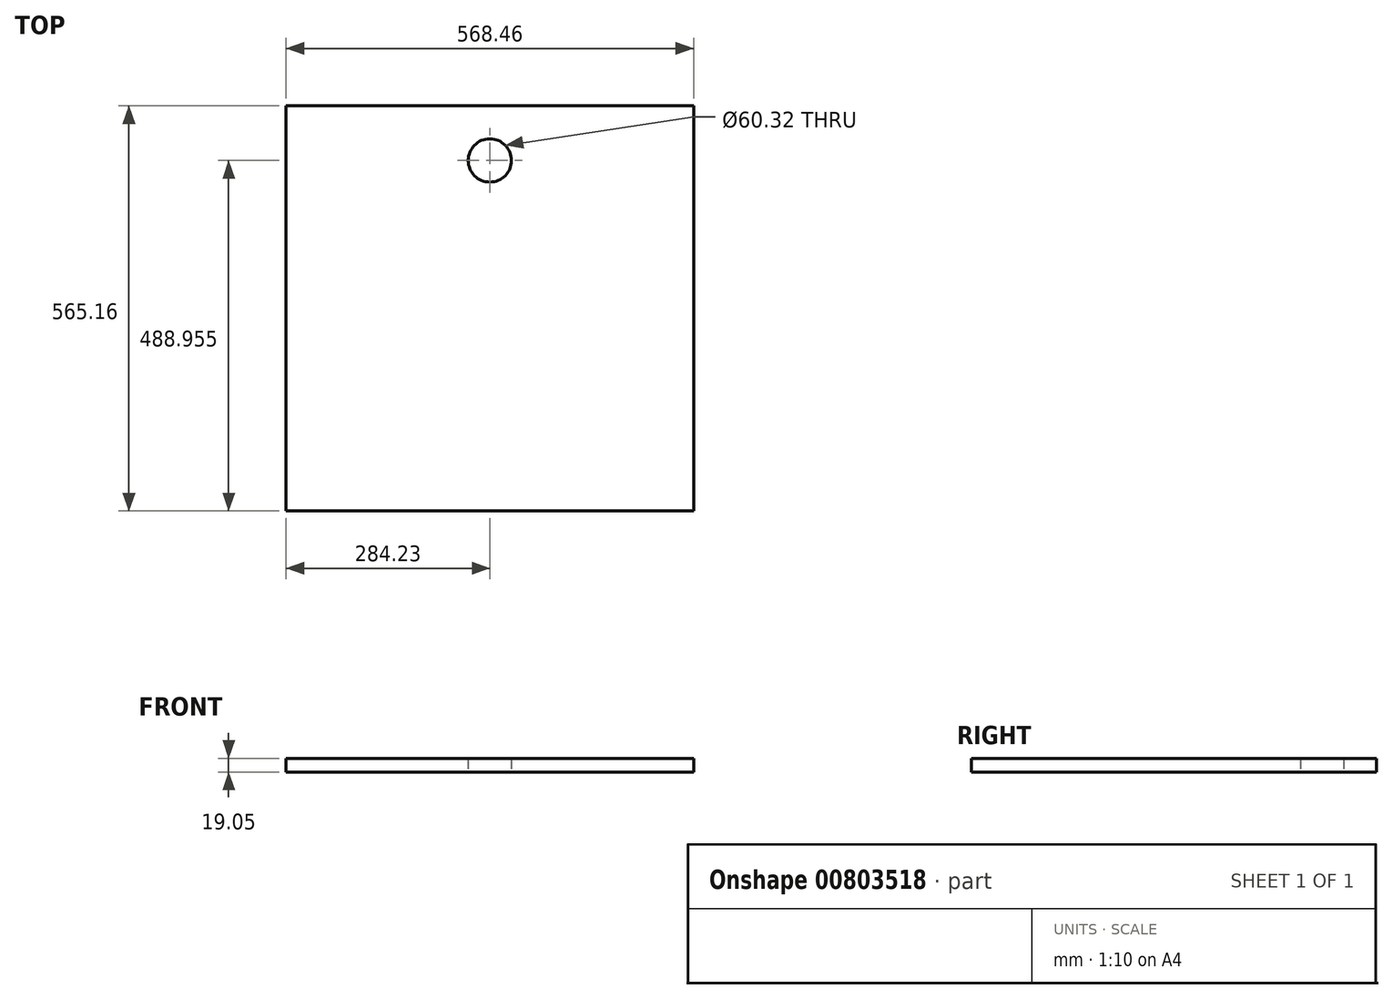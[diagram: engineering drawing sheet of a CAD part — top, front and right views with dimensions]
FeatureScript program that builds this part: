
annotation { "Feature Type Name" : "Feature", "Feature Type Description" : "" }
export const myFeature = defineFeature(function(context is Context, id is Id, definition is map)
    precondition{}
    {
        {
            var Q0;
            Q0=qCreatedBy(makeId("Top.planeOp"),FACE);
            var sketch = newSketch(context, id + "F0", { "sketchPlane" : qUnion([Q0])});
            skLineSegment(sketch, "E0.bottom", {"start": v(284.23, 282.58) * mm, "end": v(-284.23, 282.57) * mm});
            skLineSegment(sketch, "E0.top", {"start": v(284.23, -282.57) * mm, "end": v(-284.23, -282.58) * mm});
            skLineSegment(sketch, "E0.left", {"start": v(284.23, 282.58) * mm, "end": v(284.23, -282.58) * mm});
            skLineSegment(sketch, "E0.right", {"start": v(-284.23, 282.57) * mm, "end": v(-284.23, -282.58) * mm});
            skPoint(sketch, "E0.middle", {"position": v(0, 0) * mm});
            skLineSegment(sketch, "E1", {"start": v(0, 282.57) * mm, "end": v(0, 206.38) * mm});
            skCircle(sketch, "E2", {"center": v(0, 206.38) * mm, "radius": 30.16 * mm});
            skSolve(sketch);
        }
        {
            var Q0;
            Q0=makeQuery(id+"F0.imprint","IMPRINT",FACE,{"disambiguationData":[TD([[makeQuery(id+"F0.imprint","IMPRINT",EDGE,{"derivedFrom":sQuery(id+"F0.wireOp",EDGE,"E0.top")}),-1.0]])]});
            extrude(context, id + "F1", {"entities" : qUnion([Q0]), "depth" : 19.05 * mm, "offsetDistance" : 25.4 * mm});
        }
    });
